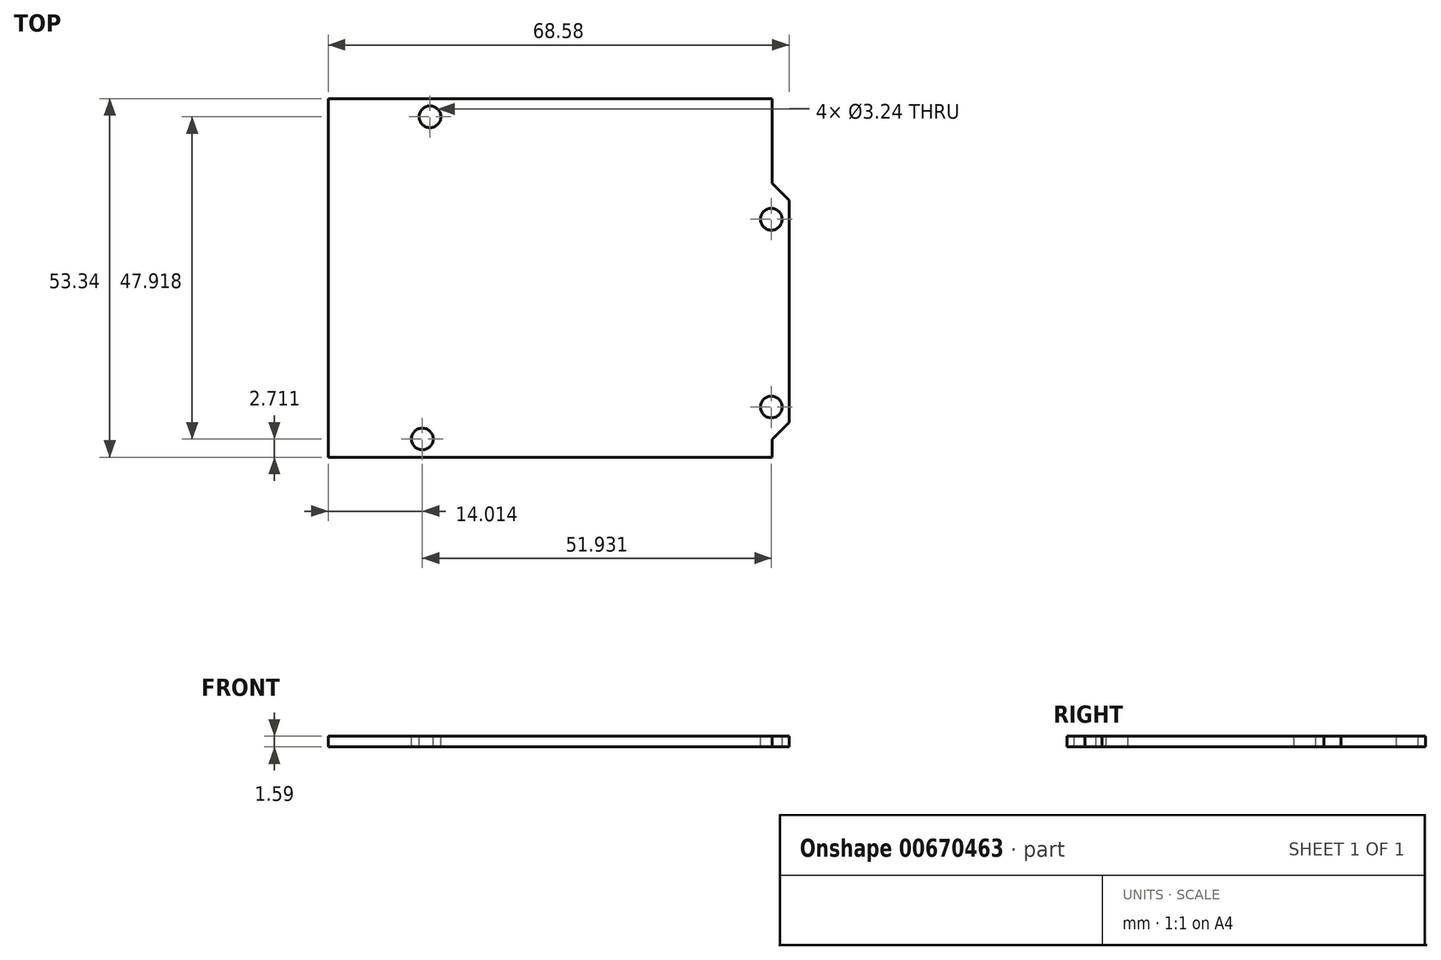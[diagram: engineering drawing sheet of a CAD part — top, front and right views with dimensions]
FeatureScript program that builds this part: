
annotation { "Feature Type Name" : "Feature", "Feature Type Description" : "" }
export const myFeature = defineFeature(function(context is Context, id is Id, definition is map)
    precondition{}
    {
        {
            var Q0;
            Q0=qCreatedBy(makeId("Top.planeOp"),FACE);
            var sketch = newSketch(context, id + "F0", { "sketchPlane" : qUnion([Q0])});
            skLineSegment(sketch, "E0", {"start": v(-33.02, 26.67) * mm, "end": v(-33.02, -26.67) * mm});
            skLineSegment(sketch, "E1", {"start": v(-33.02, -26.67) * mm, "end": v(33.02, -26.67) * mm});
            skLineSegment(sketch, "E2", {"start": v(33.02, 26.67) * mm, "end": v(-33.02, 26.67) * mm});
            skLineSegment(sketch, "E3", {"start": v(33.02, 14.1) * mm, "end": v(35.56, 11.56) * mm});
            skLineSegment(sketch, "E4", {"start": v(35.56, 11.56) * mm, "end": v(35.56, -21.46) * mm});
            skLineSegment(sketch, "E5", {"start": v(35.56, -21.46) * mm, "end": v(33.02, -24) * mm});
            skLineSegment(sketch, "E6", {"start": v(-33.02, 0) * mm, "end": v(0, 0) * mm, "construction": true});
            skPoint(sketch, "E6.endSnap0", {"position": v(0, 26.67) * mm});
            skLineSegment(sketch, "E7", {"start": v(0, 0) * mm, "end": v(0, 26.67) * mm, "construction": true});
            skLineSegment(sketch, "E8.trimOffspring", {"start": v(33.02, 14.1) * mm, "end": v(33.02, 26.67) * mm});
            skLineSegment(sketch, "E9", {"start": v(33.02, -24) * mm, "end": v(33.02, -26.67) * mm});
            skSolve(sketch);
        }
        {
            var Q0;
            Q0 = qSketchRegion(id + "F0", true);
            extrude(context, id + "F1", {"entities" : qUnion([Q0]), "depth" : 1.59 * mm, "offsetDistance" : 25 * mm});
        }
        {
            var Q0;
            Q0=makeQuery(id+"F1.opExtrude","CAP_FACE",FACE,{"disambiguationData":[OSD([sQuery(id+"F0.wireOp",EDGE,"E0"),sQuery(id+"F0.wireOp",EDGE,"E1"),sQuery(id+"F0.wireOp",EDGE,"E2"),sQuery(id+"F0.wireOp",EDGE,"E3"),sQuery(id+"F0.wireOp",EDGE,"E4"),sQuery(id+"F0.wireOp",EDGE,"E5"),sQuery(id+"F0.wireOp",EDGE,"E8.trimOffspring"),sQuery(id+"F0.wireOp",EDGE,"E9")])],"isStart":false});
            var sketch = newSketch(context, id + "F2", { "sketchPlane" : qUnion([Q0])});
            skCircle(sketch, "E10", {"center": v(-17.86, 23.96) * mm, "radius": 1.62 * mm});
            skCircle(sketch, "E11", {"center": v(32.93, 8.72) * mm, "radius": 1.62 * mm});
            skCircle(sketch, "E12", {"center": v(32.93, -19.2) * mm, "radius": 1.62 * mm});
            skCircle(sketch, "E13", {"center": v(-19, -23.96) * mm, "radius": 1.62 * mm});
            skSolve(sketch);
        }
        {
            var Q0;
            Q0=makeQuery(id+"F2.imprint","IMPRINT",FACE,{"disambiguationData":[TD([[makeQuery(id+"F2.imprint","IMPRINT",EDGE,{"derivedFrom":sQuery(id+"F2.wireOp",EDGE,"E10")}),1.0]])]});
            var Q1;
            Q1=makeQuery(id+"F2.imprint","IMPRINT",FACE,{"disambiguationData":[TD([[makeQuery(id+"F2.imprint","IMPRINT",EDGE,{"derivedFrom":sQuery(id+"F2.wireOp",EDGE,"E13")}),1.0]])]});
            var Q2;
            Q2=makeQuery(id+"F2.imprint","IMPRINT",FACE,{"disambiguationData":[TD([[makeQuery(id+"F2.imprint","IMPRINT",EDGE,{"derivedFrom":sQuery(id+"F2.wireOp",EDGE,"E12")}),1.0]])]});
            var Q3;
            Q3=makeQuery(id+"F2.imprint","IMPRINT",FACE,{"disambiguationData":[TD([[makeQuery(id+"F2.imprint","IMPRINT",EDGE,{"derivedFrom":sQuery(id+"F2.wireOp",EDGE,"E11")}),1.0]])]});
            extrude(context, id + "F3", {"entities" : qUnion([Q0, Q1, Q2, Q3]), "operationType" : NewBodyOperationType.REMOVE, "oppositeDirection" : true, "depth" : 25 * mm, "offsetDistance" : 25 * mm});
        }
    });
